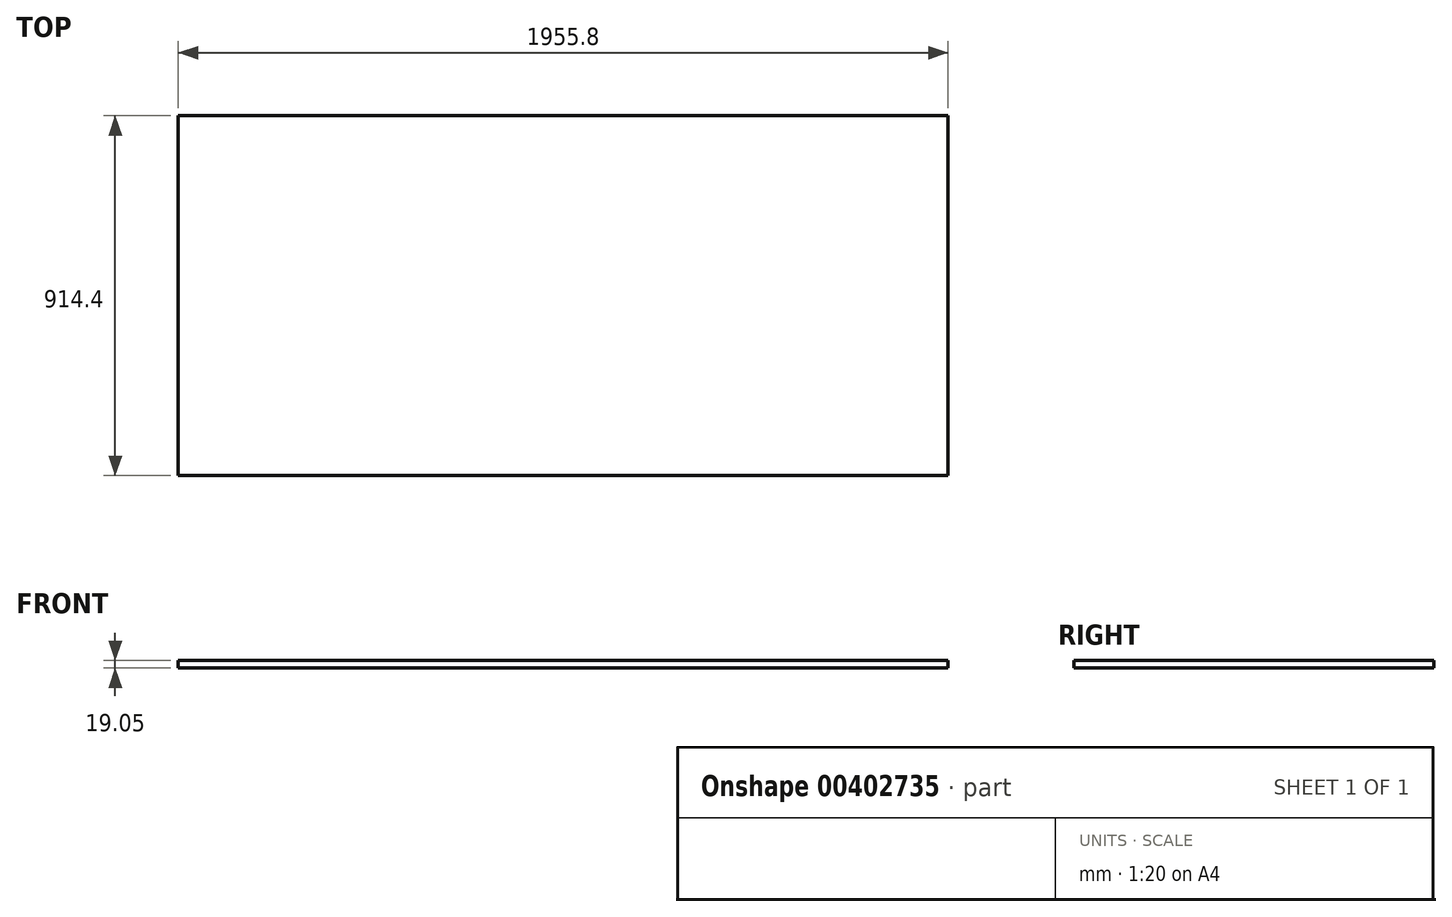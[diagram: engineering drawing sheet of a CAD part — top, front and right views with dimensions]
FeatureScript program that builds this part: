
annotation { "Feature Type Name" : "Feature", "Feature Type Description" : "" }
export const myFeature = defineFeature(function(context is Context, id is Id, definition is map)
    precondition{}
    {
        {
            var Q0;
            Q0=qCreatedBy(makeId("Top.planeOp"),FACE);
            var sketch = newSketch(context, id + "F0", { "sketchPlane" : qUnion([Q0])});
            skLineSegment(sketch, "E0.bottom", {"start": v(-1729.08, -301.09) * mm, "end": v(226.72, -301.09) * mm});
            skLineSegment(sketch, "E0.top", {"start": v(-1729.08, 613.31) * mm, "end": v(226.72, 613.31) * mm});
            skLineSegment(sketch, "E0.left", {"start": v(-1729.08, -301.09) * mm, "end": v(-1729.08, 613.31) * mm});
            skLineSegment(sketch, "E0.right", {"start": v(226.72, -301.09) * mm, "end": v(226.72, 613.31) * mm});
            skSolve(sketch);
        }
        {
            var Q0;
            Q0=makeQuery(id+"F0.imprint","IMPRINT",FACE,{"disambiguationData":[TD([[makeQuery(id+"F0.imprint","IMPRINT",EDGE,{"derivedFrom":sQuery(id+"F0.wireOp",EDGE,"E0.bottom")}),1.0]])]});
            extrude(context, id + "F1", {"entities" : qUnion([Q0]), "depth" : 19.05 * mm});
        }
    });
